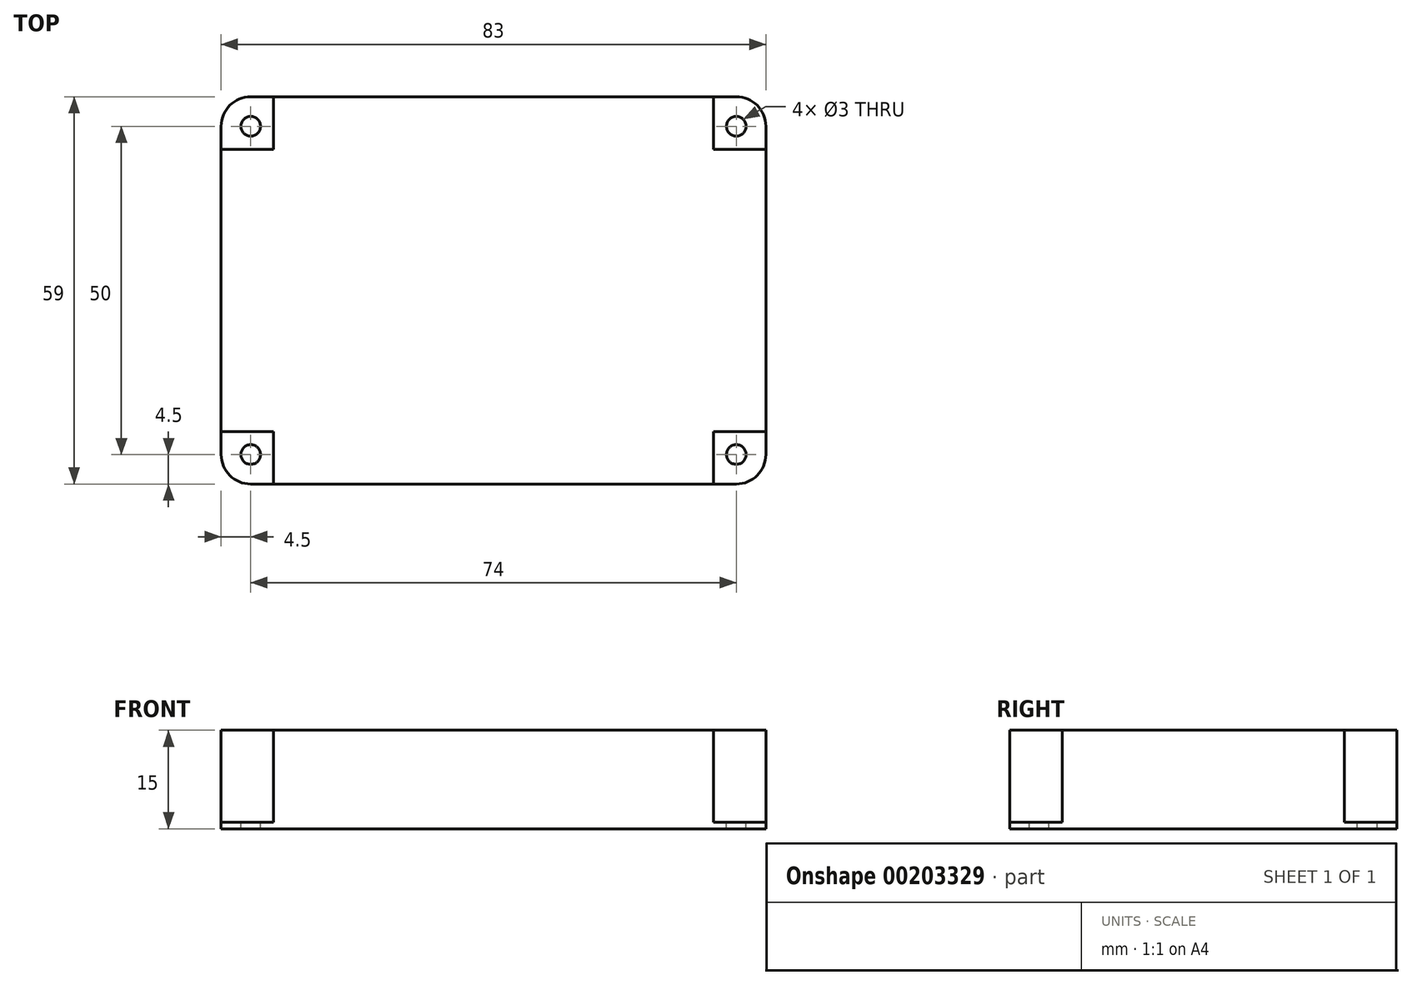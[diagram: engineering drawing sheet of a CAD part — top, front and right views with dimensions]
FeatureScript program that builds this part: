
annotation { "Feature Type Name" : "Feature", "Feature Type Description" : "" }
export const myFeature = defineFeature(function(context is Context, id is Id, definition is map)
    precondition{}
    {
        {
            var Q0;
            Q0=qCreatedBy(makeId("Top.planeOp"),FACE);
            var sketch = newSketch(context, id + "F0", { "sketchPlane" : qUnion([Q0])});
            skLineSegment(sketch, "E0.bottom", {"start": v(41.5, -29.5) * mm, "end": v(-41.5, -29.5) * mm});
            skLineSegment(sketch, "E0.top", {"start": v(41.5, 29.5) * mm, "end": v(-41.5, 29.5) * mm});
            skLineSegment(sketch, "E0.left", {"start": v(41.5, -29.5) * mm, "end": v(41.5, 29.5) * mm});
            skLineSegment(sketch, "E0.right", {"start": v(-41.5, -29.5) * mm, "end": v(-41.5, 29.5) * mm});
            skPoint(sketch, "E0.middle", {"position": v(0, 0) * mm});
            skSolve(sketch);
        }
        {
            var Q0;
            Q0 = qSketchRegion(id + "F0", true);
            extrude(context, id + "F1", {"entities" : qUnion([Q0]), "endBound" : BoundingType.SYMMETRIC, "depth" : 15 * mm});
        }
        {
            var Q0;
            Q0=makeQuery(id+"F1.opExtrude","CAP_FACE",FACE,{"disambiguationData":[OSD([sQuery(id+"F0.wireOp",EDGE,"E0.bottom"),sQuery(id+"F0.wireOp",EDGE,"E0.top"),sQuery(id+"F0.wireOp",EDGE,"E0.left"),sQuery(id+"F0.wireOp",EDGE,"E0.right")])],"isStart":false});
            var sketch = newSketch(context, id + "F2", { "sketchPlane" : qUnion([Q0])});
            skLineSegment(sketch, "E1", {"start": v(-41.5, 0) * mm, "end": v(41.5, 0) * mm, "construction": true});
            skLineSegment(sketch, "E2", {"start": v(0, 29.5) * mm, "end": v(0, -29.5) * mm, "construction": true});
            skLineSegment(sketch, "E3", {"start": v(-37, 29.5) * mm, "end": v(-37, -29.5) * mm, "construction": true});
            skCircle(sketch, "E4", {"center": v(-37, 25) * mm, "radius": 1.5 * mm});
            skCircle(sketch, "E5.MirrorC", {"center": v(37, 25) * mm, "radius": 1.5 * mm});
            skCircle(sketch, "E6.MirrorC", {"center": v(-37, -25) * mm, "radius": 1.5 * mm});
            skCircle(sketch, "E7.MirrorC", {"center": v(37, -25) * mm, "radius": 1.5 * mm});
            skSolve(sketch);
        }
        {
            var Q0;
            Q0 = qSketchRegion(id + "F2", true);
            extrude(context, id + "F3", {"entities" : qUnion([Q0]), "operationType" : NewBodyOperationType.REMOVE, "endBound" : BoundingType.THROUGH_ALL, "oppositeDirection" : true, "depth" : 25 * mm});
        }
        {
            var Q0;
            Q0=makeQuery(id+"F1.opExtrude","SWEPT_EDGE",EDGE,{"disambiguationData":[OSD([sQuery(id+"F0.wireOp",EDGE,"E0.top"),sQuery(id+"F0.wireOp",EDGE,"E0.right")])]});
            var Q1;
            Q1=makeQuery(id+"F1.opExtrude","SWEPT_EDGE",EDGE,{"disambiguationData":[OSD([sQuery(id+"F0.wireOp",EDGE,"E0.bottom"),sQuery(id+"F0.wireOp",EDGE,"E0.right")])]});
            var Q2;
            Q2=makeQuery(id+"F1.opExtrude","SWEPT_EDGE",EDGE,{"disambiguationData":[OSD([sQuery(id+"F0.wireOp",EDGE,"E0.bottom"),sQuery(id+"F0.wireOp",EDGE,"E0.left")])]});
            var Q3;
            Q3=makeQuery(id+"F1.opExtrude","SWEPT_EDGE",EDGE,{"disambiguationData":[OSD([sQuery(id+"F0.wireOp",EDGE,"E0.top"),sQuery(id+"F0.wireOp",EDGE,"E0.left")])]});
            fillet(context, id + "F4", {"entities" : qUnion([Q0, Q1, Q2, Q3]), "radius" : 4.5 * mm, "tangentPropagation" : true, "allowEdgeOverflow" : false});
        }
        {
            var Q0;
            Q0=makeQuery(id+"F1.opExtrude","CAP_FACE",FACE,{"disambiguationData":[OSD([sQuery(id+"F0.wireOp",EDGE,"E0.bottom"),sQuery(id+"F0.wireOp",EDGE,"E0.top"),sQuery(id+"F0.wireOp",EDGE,"E0.left"),sQuery(id+"F0.wireOp",EDGE,"E0.right")])],"isStart":false});
            var sketch = newSketch(context, id + "F5", { "sketchPlane" : qUnion([Q0])});
            skLineSegment(sketch, "E8.bottom", {"start": v(-33.5, 21.5) * mm, "end": v(-41.5, 21.5) * mm});
            skLineSegment(sketch, "E8.top", {"start": v(-33.5, 29.5) * mm, "end": v(-41.5, 29.5) * mm});
            skLineSegment(sketch, "E8.left", {"start": v(-33.5, 21.5) * mm, "end": v(-33.5, 29.5) * mm});
            skLineSegment(sketch, "E8.right", {"start": v(-41.5, 21.5) * mm, "end": v(-41.5, 29.5) * mm});
            skLineSegment(sketch, "E9", {"start": v(0, 29.5) * mm, "end": v(0, -29.5) * mm, "construction": true});
            skLineSegment(sketch, "E10", {"start": v(-41.5, 0) * mm, "end": v(41.5, 0) * mm, "construction": true});
            skLineSegment(sketch, "E11.MirrorCS", {"start": v(33.5, 21.5) * mm, "end": v(41.5, 21.5) * mm});
            skLineSegment(sketch, "E12.MirrorCS", {"start": v(33.5, 21.5) * mm, "end": v(33.5, 29.5) * mm});
            skLineSegment(sketch, "E13.MirrorCS", {"start": v(33.5, 29.5) * mm, "end": v(41.5, 29.5) * mm});
            skLineSegment(sketch, "E14.MirrorCS", {"start": v(41.5, 21.5) * mm, "end": v(41.5, 29.5) * mm});
            skLineSegment(sketch, "E15.MirrorCS", {"start": v(-33.5, -21.5) * mm, "end": v(-41.5, -21.5) * mm});
            skLineSegment(sketch, "E16.MirrorCS", {"start": v(-33.5, -21.5) * mm, "end": v(-33.5, -29.5) * mm});
            skLineSegment(sketch, "E17.MirrorCS", {"start": v(-33.5, -29.5) * mm, "end": v(-41.5, -29.5) * mm});
            skLineSegment(sketch, "E18.MirrorCS", {"start": v(-41.5, -21.5) * mm, "end": v(-41.5, -29.5) * mm});
            skLineSegment(sketch, "E19.MirrorCS", {"start": v(33.5, -21.5) * mm, "end": v(41.5, -21.5) * mm});
            skLineSegment(sketch, "E20.MirrorCS", {"start": v(33.5, -21.5) * mm, "end": v(33.5, -29.5) * mm});
            skLineSegment(sketch, "E21.MirrorCS", {"start": v(41.5, -21.5) * mm, "end": v(41.5, -29.5) * mm});
            skLineSegment(sketch, "E22.MirrorCS", {"start": v(33.5, -29.5) * mm, "end": v(41.5, -29.5) * mm});
            skSolve(sketch);
        }
        {
            var Q0;
            Q0 = qSketchRegion(id + "F5", true);
            extrude(context, id + "F6", {"entities" : qUnion([Q0]), "operationType" : NewBodyOperationType.REMOVE, "oppositeDirection" : true, "depth" : 14 * mm});
        }
    });
